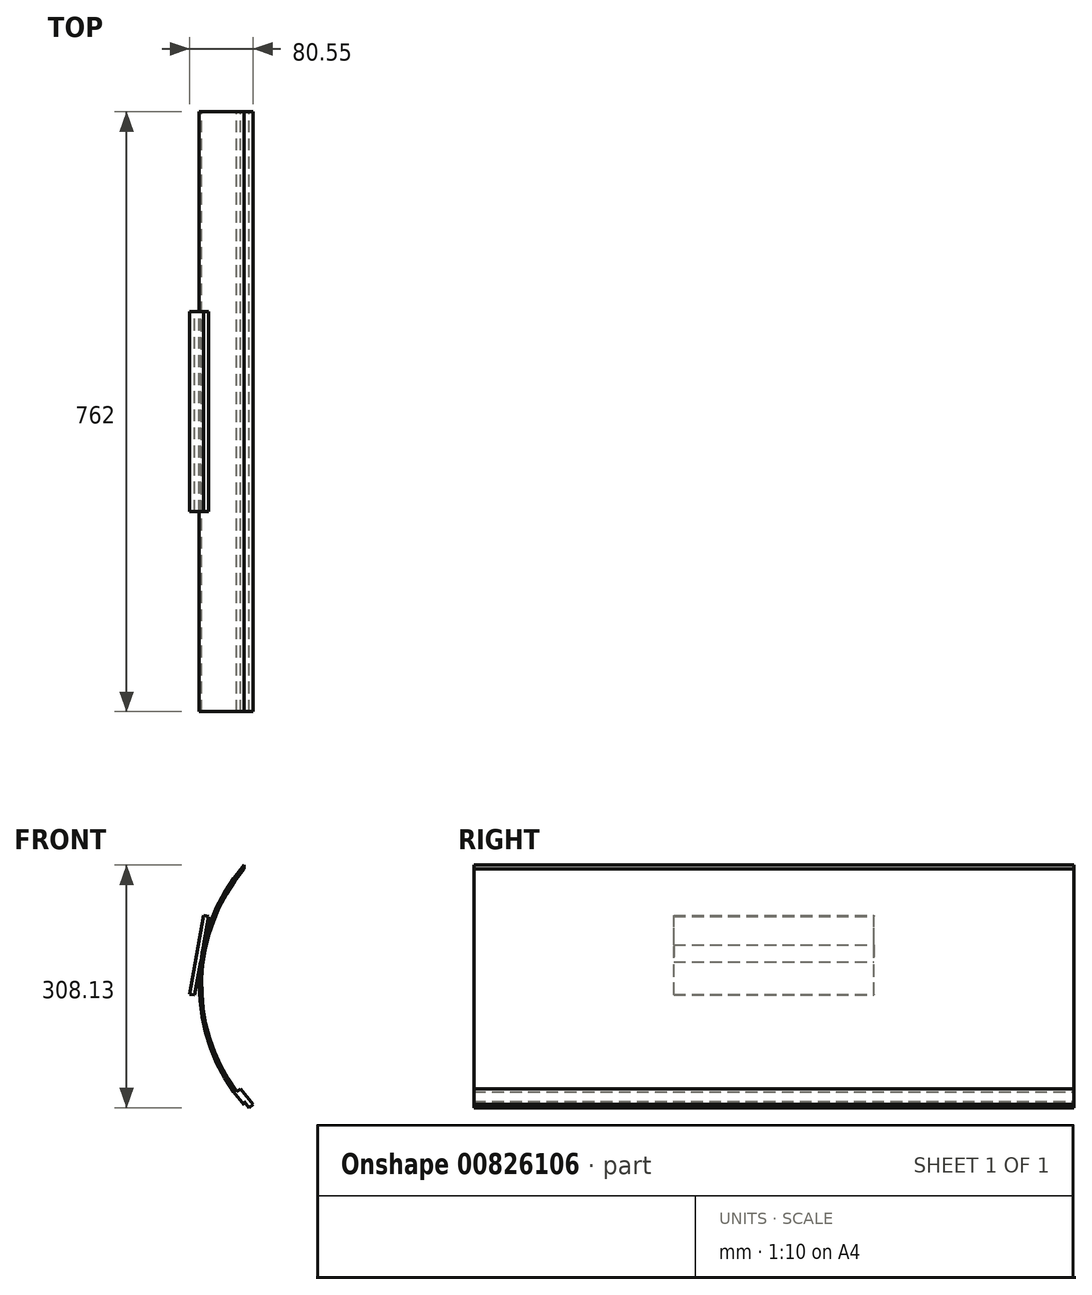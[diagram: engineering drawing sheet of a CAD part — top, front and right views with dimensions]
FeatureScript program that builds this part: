
annotation { "Feature Type Name" : "Feature", "Feature Type Description" : "" }
export const myFeature = defineFeature(function(context is Context, id is Id, definition is map)
    precondition{}
    {
        {
            var Q0;
            Q0=qCreatedBy(makeId("Front.planeOp"),FACE);
            var sketch = newSketch(context, id + "F0", { "sketchPlane" : qUnion([Q0])});
            skArc(sketch, "E0", {"start": v(-174.63, 147.53) * mm, "mid": v(-228.6, 0) * mm, "end": v(-174.63, -147.53) * mm});
            skArc(sketch, "E1.0", {"start": v(-174.63, 152.4) * mm, "mid": v(-231.78, 0) * mm, "end": v(-174.63, -152.4) * mm});
            skLineSegment(sketch, "E2", {"start": v(-174.63, 152.4) * mm, "end": v(-174.63, 147.53) * mm});
            skLineSegment(sketch, "E3.trimOffspring", {"start": v(-174.63, -147.53) * mm, "end": v(-174.63, -152.4) * mm});
            skSolve(sketch);
        }
        {
            var Q0;
            Q0=qSketchRegion(id+"F0",true);
            extrude(context, id + "F1", {"entities" : qUnion([Q0]), "endBound" : BoundingType.SYMMETRIC, "depth" : 762 * mm, "offsetDistance" : 25.4 * mm});
        }
        {
            var Q0;
            Q0=qCreatedBy(makeId("Front.planeOp"),FACE);
            var sketch = newSketch(context, id + "F2", { "sketchPlane" : qUnion([Q0])});
            skArc(sketch, "E4.0", {"start": v(-174.63, 152.4) * mm, "mid": v(-231.78, 0) * mm, "end": v(-174.63, -152.4) * mm, "construction": true});
            skLineSegment(sketch, "E5", {"start": v(-237.59, -12.7) * mm, "end": v(-219.95, 87.36) * mm, "construction": true});
            skLineSegment(sketch, "E6", {"start": v(0, 0) * mm, "end": v(-285.96, 0) * mm, "construction": true});
            skLineSegment(sketch, "E7.0", {"start": v(-243.84, -11.6) * mm, "end": v(-226.2, 88.46) * mm});
            skLineSegment(sketch, "E8", {"start": v(-226.2, 88.46) * mm, "end": v(-219.7, 87.31) * mm});
            skLineSegment(sketch, "E9", {"start": v(-243.84, -11.6) * mm, "end": v(-237.34, -12.74) * mm});
            skLineSegment(sketch, "E10.0", {"start": v(-237.34, -12.74) * mm, "end": v(-219.7, 87.31) * mm});
            skSolve(sketch);
        }
        {
            var Q0;
            Q0=makeQuery(id+"F2.imprint","IMPRINT",FACE,{"disambiguationData":[TD([[makeQuery(id+"F2.imprint","IMPRINT",EDGE,{"derivedFrom":sQuery(id+"F2.wireOp",EDGE,"E5")}),1.0]])]});
            var Q1;
            Q1=makeQuery(id+"F2.imprint","IMPRINT",FACE,{"disambiguationData":[TD([[makeQuery(id+"F2.imprint","IMPRINT",EDGE,{"derivedFrom":sQuery(id+"F2.wireOp",EDGE,"E7.0")}),-1.0]])]});
            extrude(context, id + "F3", {"entities" : qUnion([Q0, Q1]), "operationType" : NewBodyOperationType.ADD, "endBound" : BoundingType.SYMMETRIC, "depth" : 254 * mm, "offsetDistance" : 25.4 * mm});
        }
        {
            var Q0;
            Q0=qCreatedBy(makeId("Front.planeOp"),FACE);
            var sketch = newSketch(context, id + "F4", { "sketchPlane" : qUnion([Q0])});
            skLineSegment(sketch, "E11", {"start": v(-168.27, -155.58) * mm, "end": v(-184.01, -135.64) * mm, "construction": true});
            skLineSegment(sketch, "E12.0", {"start": v(-174.63, -147.53) * mm, "end": v(-174.63, -152.4) * mm, "construction": true});
            skArc(sketch, "E13.0", {"start": v(-174.63, 147.53) * mm, "mid": v(-228.6, 0) * mm, "end": v(-174.63, -147.53) * mm, "construction": true});
            skLineSegment(sketch, "E14", {"start": v(-174.63, -152.4) * mm, "end": v(-168.91, -152.4) * mm, "construction": true});
            skLineSegment(sketch, "E15.0", {"start": v(-163.29, -151.64) * mm, "end": v(-179.03, -131.7) * mm});
            skLineSegment(sketch, "E16", {"start": v(-184.2, -135.8) * mm, "end": v(-179.03, -131.7) * mm});
            skLineSegment(sketch, "E17", {"start": v(-168.47, -155.73) * mm, "end": v(-163.29, -151.64) * mm});
            skLineSegment(sketch, "E18.0", {"start": v(-163.29, -151.64) * mm, "end": v(-179.03, -131.7) * mm, "construction": true});
            skLineSegment(sketch, "E19.0", {"start": v(-168.47, -155.73) * mm, "end": v(-184.2, -135.8) * mm});
            skSolve(sketch);
        }
        {
            var Q0;
            Q0=qSketchRegion(id+"F4",true);
            extrude(context, id + "F5", {"entities" : qUnion([Q0]), "operationType" : NewBodyOperationType.ADD, "endBound" : BoundingType.SYMMETRIC, "depth" : 762 * mm, "offsetDistance" : 25.4 * mm});
        }
    });
